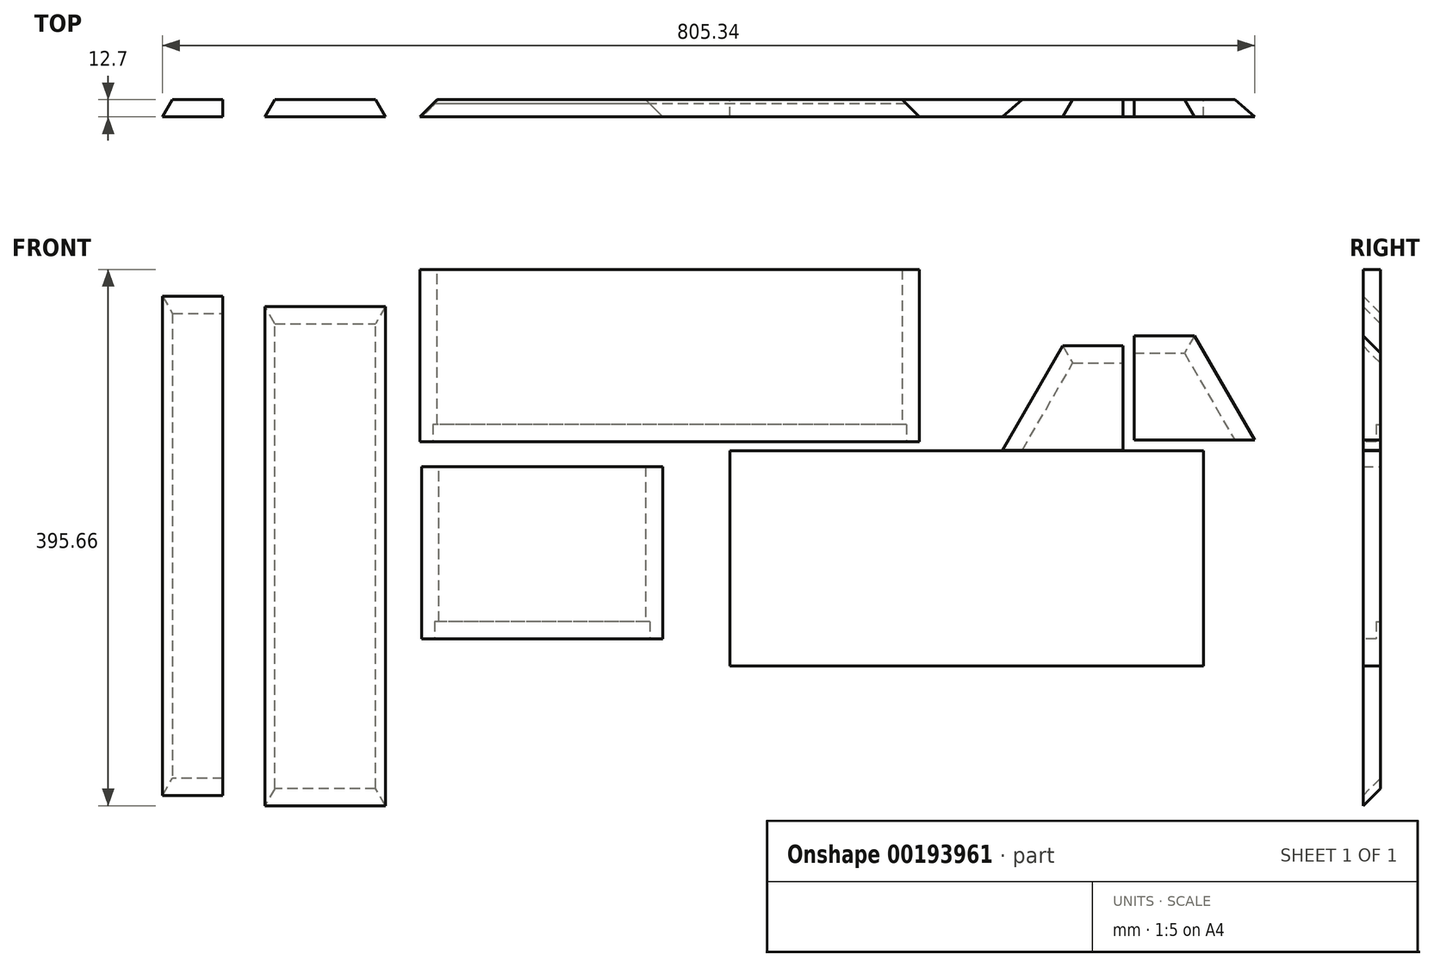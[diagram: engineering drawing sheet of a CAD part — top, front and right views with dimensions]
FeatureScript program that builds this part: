
annotation { "Feature Type Name" : "Feature", "Feature Type Description" : "" }
export const myFeature = defineFeature(function(context is Context, id is Id, definition is map)
    precondition{}
    {
        {
            var Q0;
            Q0=qCreatedBy(makeId("Front.planeOp"),FACE);
            var sketch = newSketch(context, id + "F0", { "sketchPlane" : qUnion([Q0])});
            skLineSegment(sketch, "E0.bottom", {"start": v(-232.35, 116.13) * mm, "end": v(135.95, 116.13) * mm});
            skLineSegment(sketch, "E0.top", {"start": v(-232.35, -10.87) * mm, "end": v(135.95, -10.87) * mm});
            skLineSegment(sketch, "E0.left", {"start": v(-232.35, 116.13) * mm, "end": v(-232.35, -10.87) * mm});
            skLineSegment(sketch, "E0.right", {"start": v(135.95, 116.13) * mm, "end": v(135.95, -10.87) * mm});
            skSolve(sketch);
        }
        {
            var Q0;
            Q0=makeQuery(id+"F0.imprint","IMPRINT",FACE,{"disambiguationData":[TD([[makeQuery(id+"F0.imprint","IMPRINT",EDGE,{"derivedFrom":sQuery(id+"F0.wireOp",EDGE,"E0.bottom")}),-1.0]])]});
            extrude(context, id + "F1", {"entities" : qUnion([Q0]), "depth" : 12.7 * mm});
        }
        {
            var Q0;
            Q0=qCreatedBy(makeId("Front.planeOp"),FACE);
            var sketch = newSketch(context, id + "F2", { "sketchPlane" : qUnion([Q0])});
            skLineSegment(sketch, "E1.bottom", {"start": v(-230.99, -29.36) * mm, "end": v(-53.19, -29.36) * mm});
            skLineSegment(sketch, "E1.top", {"start": v(-230.99, -156.36) * mm, "end": v(-53.19, -156.36) * mm});
            skLineSegment(sketch, "E1.left", {"start": v(-230.99, -29.36) * mm, "end": v(-230.99, -156.36) * mm});
            skLineSegment(sketch, "E1.right", {"start": v(-53.19, -29.36) * mm, "end": v(-53.19, -156.36) * mm});
            skSolve(sketch);
        }
        {
            var Q0;
            Q0=makeQuery(id+"F2.imprint","IMPRINT",FACE,{"disambiguationData":[TD([[makeQuery(id+"F2.imprint","IMPRINT",EDGE,{"derivedFrom":sQuery(id+"F2.wireOp",EDGE,"E1.bottom")}),-1.0]])]});
            extrude(context, id + "F3", {"entities" : qUnion([Q0]), "depth" : 12.7 * mm});
        }
        {
            var Q0;
            Q0=makeQuery(id+"F1.opExtrude","CAP_EDGE",EDGE,{"disambiguationData":[OSD([sQuery(id+"F0.wireOp",EDGE,"E0.right")])],"isStart":true});
            chamfer(context, id + "F4", {"entities" : qUnion([Q0]), "width" : 12.7 * mm, "tangentPropagation" : true});
        }
        {
            var Q0;
            Q0=makeQuery(id+"F3.opExtrude","CAP_EDGE",EDGE,{"disambiguationData":[OSD([sQuery(id+"F2.wireOp",EDGE,"E1.right")])],"isStart":true});
            chamfer(context, id + "F5", {"entities" : qUnion([Q0]), "width" : 12.7 * mm, "tangentPropagation" : true});
        }
        {
            var Q0;
            Q0=makeQuery(id+"F1.opExtrude","SWEPT_FACE",FACE,{"disambiguationData":[OSD([sQuery(id+"F0.wireOp",EDGE,"E0.left")])]});
            var sketch = newSketch(context, id + "F6", { "sketchPlane" : qUnion([Q0])});
            skLineSegment(sketch, "E2.bottom", {"start": v(0, -10.87) * mm, "end": v(3.18, -10.87) * mm});
            skLineSegment(sketch, "E2.top", {"start": v(0, 1.83) * mm, "end": v(3.17, 1.83) * mm});
            skLineSegment(sketch, "E2.left", {"start": v(0, -10.87) * mm, "end": v(0, 1.83) * mm});
            skLineSegment(sketch, "E2.right", {"start": v(3.18, -10.87) * mm, "end": v(3.17, 1.83) * mm});
            skSolve(sketch);
        }
        {
            var Q0;
            Q0=makeQuery(id+"F6.imprint","IMPRINT",FACE,{"disambiguationData":[TD([[makeQuery(id+"F6.imprint","IMPRINT",EDGE,{"derivedFrom":sQuery(id+"F6.wireOp",EDGE,"E2.bottom")}),-1.0]])]});
            extrude(context, id + "F7", {"entities" : qUnion([Q0]), "operationType" : NewBodyOperationType.REMOVE, "oppositeDirection" : true, "depth" : 368.3 * mm});
        }
        {
            var Q0;
            Q0=makeQuery(id+"F3.opExtrude","SWEPT_FACE",FACE,{"disambiguationData":[OSD([sQuery(id+"F2.wireOp",EDGE,"E1.left")])]});
            var sketch = newSketch(context, id + "F8", { "sketchPlane" : qUnion([Q0])});
            skLineSegment(sketch, "E3.bottom", {"start": v(0, -156.36) * mm, "end": v(3.18, -156.36) * mm});
            skLineSegment(sketch, "E3.top", {"start": v(0, -143.66) * mm, "end": v(3.17, -143.66) * mm});
            skLineSegment(sketch, "E3.left", {"start": v(0, -156.36) * mm, "end": v(0, -143.66) * mm});
            skLineSegment(sketch, "E3.right", {"start": v(3.18, -156.36) * mm, "end": v(3.17, -143.66) * mm});
            skSolve(sketch);
        }
        {
            var Q0;
            Q0=makeQuery(id+"F8.imprint","IMPRINT",FACE,{"disambiguationData":[TD([[makeQuery(id+"F8.imprint","IMPRINT",EDGE,{"derivedFrom":sQuery(id+"F8.wireOp",EDGE,"E3.bottom")}),-1.0]])]});
            extrude(context, id + "F9", {"entities" : qUnion([Q0]), "operationType" : NewBodyOperationType.REMOVE, "oppositeDirection" : true, "depth" : 368.3 * mm});
        }
        {
            var Q0;
            Q0=makeQuery(id+"F1.opExtrude","CAP_EDGE",EDGE,{"disambiguationData":[OSD([sQuery(id+"F0.wireOp",EDGE,"E0.left")])],"isStart":true});
            chamfer(context, id + "F10", {"entities" : qUnion([Q0]), "width" : 12.7 * mm, "tangentPropagation" : true});
        }
        {
            var Q0;
            Q0=makeQuery(id+"F3.opExtrude","CAP_EDGE",EDGE,{"disambiguationData":[OSD([sQuery(id+"F2.wireOp",EDGE,"E1.left")])],"isStart":true});
            chamfer(context, id + "F11", {"entities" : qUnion([Q0]), "width" : 12.7 * mm, "tangentPropagation" : true});
        }
        {
            var Q0;
            Q0=qCreatedBy(makeId("Front.planeOp"),FACE);
            var sketch = newSketch(context, id + "F12", { "sketchPlane" : qUnion([Q0])});
            skLineSegment(sketch, "E4.bottom", {"start": v(-3.84, -17.72) * mm, "end": v(345.4, -17.72) * mm});
            skLineSegment(sketch, "E4.top", {"start": v(-3.84, -176.47) * mm, "end": v(345.4, -176.47) * mm});
            skLineSegment(sketch, "E4.left", {"start": v(-3.84, -17.72) * mm, "end": v(-3.84, -176.47) * mm});
            skLineSegment(sketch, "E4.right", {"start": v(345.4, -17.72) * mm, "end": v(345.4, -176.47) * mm});
            skSolve(sketch);
        }
        {
            var Q0;
            Q0=makeQuery(id+"F12.imprint","IMPRINT",FACE,{"disambiguationData":[TD([[makeQuery(id+"F12.imprint","IMPRINT",EDGE,{"derivedFrom":sQuery(id+"F12.wireOp",EDGE,"E4.bottom")}),-1.0]])]});
            extrude(context, id + "F13", {"entities" : qUnion([Q0]), "depth" : 12.7 * mm});
        }
        {
            var Q0;
            Q0=qCreatedBy(makeId("Front.planeOp"),FACE);
            var sketch = newSketch(context, id + "F14", { "sketchPlane" : qUnion([Q0])});
            skLineSegment(sketch, "E5.bottom", {"start": v(-422.15, 96.36) * mm, "end": v(-377.7, 96.36) * mm});
            skLineSegment(sketch, "E5.top", {"start": v(-422.15, -271.94) * mm, "end": v(-377.7, -271.94) * mm});
            skLineSegment(sketch, "E5.left", {"start": v(-422.15, 96.36) * mm, "end": v(-422.15, -271.94) * mm});
            skLineSegment(sketch, "E5.right", {"start": v(-377.7, 96.36) * mm, "end": v(-377.7, -271.94) * mm});
            skSolve(sketch);
        }
        {
            var Q0;
            Q0=makeQuery(id+"F14.imprint","IMPRINT",FACE,{"disambiguationData":[TD([[makeQuery(id+"F14.imprint","IMPRINT",EDGE,{"derivedFrom":sQuery(id+"F14.wireOp",EDGE,"E5.bottom")}),-1.0]])]});
            extrude(context, id + "F15", {"entities" : qUnion([Q0]), "depth" : 12.7 * mm});
        }
        {
            var Q0;
            Q0=qCreatedBy(makeId("Front.planeOp"),FACE);
            var sketch = newSketch(context, id + "F16", { "sketchPlane" : qUnion([Q0])});
            skLineSegment(sketch, "E6", {"start": v(294.3, -9.8) * mm, "end": v(383.2, -9.8) * mm});
            skLineSegment(sketch, "E7", {"start": v(383.2, -9.8) * mm, "end": v(338.74, 67.18) * mm});
            skLineSegment(sketch, "E8", {"start": v(338.74, 67.18) * mm, "end": v(294.3, 67.18) * mm});
            skLineSegment(sketch, "E9", {"start": v(294.3, 67.18) * mm, "end": v(294.3, -9.8) * mm});
            skPoint(sketch, "E10.start.orphan", {"position": v(249.84, 67.18) * mm});
            skPoint(sketch, "E11.start.orphan", {"position": v(205.4, -9.8) * mm});
            skSolve(sketch);
        }
        {
            var Q0;
            Q0=makeQuery(id+"F16.imprint","IMPRINT",FACE,{"disambiguationData":[TD([[makeQuery(id+"F16.imprint","IMPRINT",EDGE,{"derivedFrom":sQuery(id+"F16.wireOp",EDGE,"E6")}),1.0]])]});
            extrude(context, id + "F17", {"entities" : qUnion([Q0]), "depth" : 12.7 * mm});
        }
        {
            var Q0;
            Q0=makeQuery(id+"F17.opExtrude","CAP_EDGE",EDGE,{"disambiguationData":[OSD([sQuery(id+"F16.wireOp",EDGE,"E7")])],"isStart":true});
            var Q1;
            Q1=makeQuery(id+"F17.opExtrude","CAP_EDGE",EDGE,{"disambiguationData":[OSD([sQuery(id+"F16.wireOp",EDGE,"E8")])],"isStart":true});
            var Q2;
            Q2=makeQuery(id+"F17.opExtrude","CAP_EDGE",EDGE,{"disambiguationData":[OSD([sQuery(id+"F16.wireOp",EDGE,"E10")])],"isStart":true});
            chamfer(context, id + "F18", {"entities" : qUnion([Q0, Q1, Q2]), "width" : 12.7 * mm, "tangentPropagation" : true});
        }
        {
            var Q0;
            Q0=makeQuery(id+"F15.opExtrude","SWEPT_FACE",FACE,{"disambiguationData":[OSD([sQuery(id+"F14.wireOp",EDGE,"E5.top")])]});
            var sketch = newSketch(context, id + "F19", { "sketchPlane" : qUnion([Q0])});
            skLineSegment(sketch, "E12", {"start": v(-422.15, 12.7) * mm, "end": v(-422.15, 0) * mm});
            skLineSegment(sketch, "E13", {"start": v(-422.15, 0) * mm, "end": v(-414.82, 0) * mm});
            skLineSegment(sketch, "E14", {"start": v(-414.82, 0) * mm, "end": v(-422.15, 12.7) * mm});
            skSolve(sketch);
        }
        {
            var Q0;
            Q0=makeQuery(id+"F19.imprint","IMPRINT",FACE,{"disambiguationData":[TD([[makeQuery(id+"F19.imprint","IMPRINT",EDGE,{"derivedFrom":sQuery(id+"F19.wireOp",EDGE,"E12")}),1.0]])]});
            var Q1;
            Q1=makeQuery(id+"F19.imprint","IMPRINT",FACE,{"disambiguationData":[TD([[makeQuery(id+"F19.imprint","IMPRINT",EDGE,{"derivedFrom":sQuery(id+"F19.wireOp",EDGE,"HloDxKfB-YmLV-lAdB-1i6o-Y0Wx5UDSzw0H")}),-1.0]])]});
            extrude(context, id + "F20", {"entities" : qUnion([Q0, Q1]), "operationType" : NewBodyOperationType.REMOVE, "oppositeDirection" : true, "depth" : 368.3 * mm});
        }
        {
            var Q0;
            Q0=makeQuery(id+"F15.opExtrude","CAP_EDGE",EDGE,{"disambiguationData":[OSD([sQuery(id+"F14.wireOp",EDGE,"E5.bottom")])],"isStart":true});
            var Q1;
            Q1=makeQuery(id+"F15.opExtrude","CAP_EDGE",EDGE,{"disambiguationData":[OSD([sQuery(id+"F14.wireOp",EDGE,"E5.top")])],"isStart":true});
            chamfer(context, id + "F21", {"entities" : qUnion([Q0, Q1]), "width" : 12.7 * mm, "tangentPropagation" : true});
        }
        {
            var Q0;
            Q0=qCreatedBy(makeId("Front.planeOp"),FACE);
            var sketch = newSketch(context, id + "F22", { "sketchPlane" : qUnion([Q0])});
            skLineSegment(sketch, "E15.bottom", {"start": v(-257.73, 88.77) * mm, "end": v(-346.63, 88.77) * mm});
            skLineSegment(sketch, "E15.top", {"start": v(-257.73, -279.53) * mm, "end": v(-346.63, -279.53) * mm});
            skLineSegment(sketch, "E15.left", {"start": v(-257.73, 88.77) * mm, "end": v(-257.73, -279.53) * mm});
            skLineSegment(sketch, "E15.right", {"start": v(-346.63, 88.77) * mm, "end": v(-346.63, -279.53) * mm});
            skSolve(sketch);
        }
        {
            var Q0;
            Q0=makeQuery(id+"F22.imprint","IMPRINT",FACE,{"disambiguationData":[TD([[makeQuery(id+"F22.imprint","IMPRINT",EDGE,{"derivedFrom":sQuery(id+"F22.wireOp",EDGE,"E15.bottom")}),1.0]])]});
            extrude(context, id + "F23", {"entities" : qUnion([Q0]), "depth" : 12.7 * mm});
        }
        {
            var Q0;
            Q0=makeQuery(id+"F23.opExtrude","SWEPT_FACE",FACE,{"disambiguationData":[OSD([sQuery(id+"F22.wireOp",EDGE,"E15.bottom")])]});
            var sketch = newSketch(context, id + "F24", { "sketchPlane" : qUnion([Q0])});
            skLineSegment(sketch, "E16", {"start": v(-346.63, -12.7) * mm, "end": v(-346.63, 0) * mm});
            skLineSegment(sketch, "E17", {"start": v(-346.63, 0) * mm, "end": v(-339.3, 0) * mm});
            skLineSegment(sketch, "E18", {"start": v(-339.3, 0) * mm, "end": v(-346.63, -12.7) * mm});
            skLineSegment(sketch, "E19", {"start": v(-257.73, -12.7) * mm, "end": v(-257.73, 0) * mm});
            skLineSegment(sketch, "E20", {"start": v(-257.73, 0) * mm, "end": v(-265.07, 0) * mm});
            skLineSegment(sketch, "E21", {"start": v(-265.07, 0) * mm, "end": v(-257.73, -12.7) * mm});
            skSolve(sketch);
        }
        {
            var Q0;
            Q0=makeQuery(id+"F24.imprint","IMPRINT",FACE,{"disambiguationData":[TD([[makeQuery(id+"F24.imprint","IMPRINT",EDGE,{"derivedFrom":sQuery(id+"F24.wireOp",EDGE,"E16")}),-1.0]])]});
            var Q1;
            Q1=makeQuery(id+"F24.imprint","IMPRINT",FACE,{"disambiguationData":[TD([[makeQuery(id+"F24.imprint","IMPRINT",EDGE,{"derivedFrom":sQuery(id+"F24.wireOp",EDGE,"E19")}),1.0]])]});
            extrude(context, id + "F25", {"entities" : qUnion([Q0, Q1]), "operationType" : NewBodyOperationType.REMOVE, "oppositeDirection" : true, "depth" : 368.3 * mm});
        }
        {
            var Q0;
            Q0=qCreatedBy(makeId("Front.planeOp"),FACE);
            var sketch = newSketch(context, id + "F26", { "sketchPlane" : qUnion([Q0])});
            skLineSegment(sketch, "E22", {"start": v(286.13, -17.3) * mm, "end": v(197.23, -17.3) * mm});
            skLineSegment(sketch, "E23", {"start": v(197.23, -17.3) * mm, "end": v(241.68, 59.7) * mm});
            skLineSegment(sketch, "E24", {"start": v(241.68, 59.7) * mm, "end": v(286.13, 59.7) * mm});
            skLineSegment(sketch, "E25", {"start": v(286.13, 59.7) * mm, "end": v(286.13, -17.3) * mm});
            skSolve(sketch);
        }
        {
            var Q0;
            Q0=makeQuery(id+"F26.imprint","IMPRINT",FACE,{"disambiguationData":[TD([[makeQuery(id+"F26.imprint","IMPRINT",EDGE,{"derivedFrom":sQuery(id+"F26.wireOp",EDGE,"E22")}),-1.0]])]});
            extrude(context, id + "F27", {"entities" : qUnion([Q0]), "depth" : 12.7 * mm});
        }
        {
            var Q0;
            Q0=makeQuery(id+"F27.opExtrude","CAP_EDGE",EDGE,{"disambiguationData":[OSD([sQuery(id+"F26.wireOp",EDGE,"E23")])],"isStart":true});
            var Q1;
            Q1=makeQuery(id+"F27.opExtrude","CAP_EDGE",EDGE,{"disambiguationData":[OSD([sQuery(id+"F26.wireOp",EDGE,"E24")])],"isStart":true});
            chamfer(context, id + "F28", {"entities" : qUnion([Q0, Q1]), "width" : 12.7 * mm, "tangentPropagation" : true});
        }
        {
            var Q0;
            Q0=makeQuery(id+"F23.opExtrude","CAP_EDGE",EDGE,{"disambiguationData":[OSD([sQuery(id+"F22.wireOp",EDGE,"E15.bottom")])],"isStart":true});
            var Q1;
            Q1=makeQuery(id+"F23.opExtrude","CAP_EDGE",EDGE,{"disambiguationData":[OSD([sQuery(id+"F22.wireOp",EDGE,"E15.top")])],"isStart":true});
            chamfer(context, id + "F29", {"entities" : qUnion([Q0, Q1]), "width" : 12.7 * mm, "tangentPropagation" : true});
        }
    });
